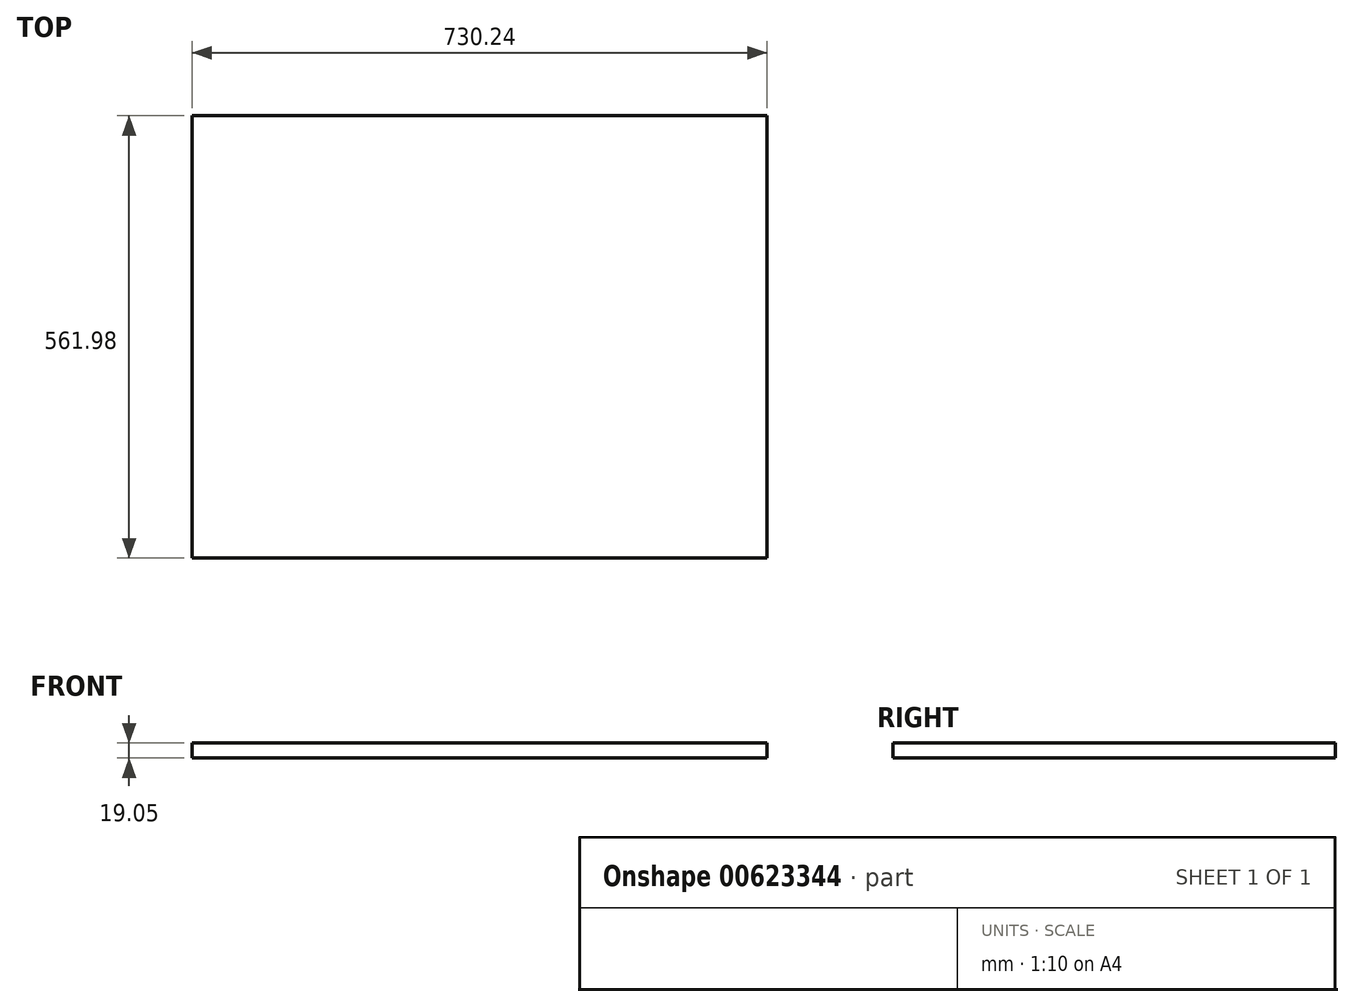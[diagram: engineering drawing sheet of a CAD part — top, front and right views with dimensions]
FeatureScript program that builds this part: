
annotation { "Feature Type Name" : "Feature", "Feature Type Description" : "" }
export const myFeature = defineFeature(function(context is Context, id is Id, definition is map)
    precondition{}
    {
        {
            var Q0;
            Q0=qCreatedBy(makeId("Top.planeOp"),FACE);
            var sketch = newSketch(context, id + "F0", { "sketchPlane" : qUnion([Q0])});
            skLineSegment(sketch, "E0.bottom", {"start": v(-365.12, 280.99) * mm, "end": v(365.13, 280.99) * mm});
            skLineSegment(sketch, "E0.top", {"start": v(-365.13, -280.99) * mm, "end": v(365.12, -280.99) * mm});
            skLineSegment(sketch, "E0.left", {"start": v(-365.12, 280.99) * mm, "end": v(-365.13, -280.99) * mm});
            skLineSegment(sketch, "E0.right", {"start": v(365.13, 280.99) * mm, "end": v(365.13, -280.99) * mm});
            skPoint(sketch, "E0.middle", {"position": v(0, 0) * mm});
            skSolve(sketch);
        }
        {
            var Q0;
            Q0=makeQuery(id+"F0.imprint","IMPRINT",FACE,{"disambiguationData":[TD([[makeQuery(id+"F0.imprint","IMPRINT",EDGE,{"derivedFrom":sQuery(id+"F0.wireOp",EDGE,"E0.bottom")}),-1.0]])]});
            extrude(context, id + "F1", {"entities" : qUnion([Q0]), "depth" : 19.05 * mm, "offsetDistance" : 25.4 * mm});
        }
    });
